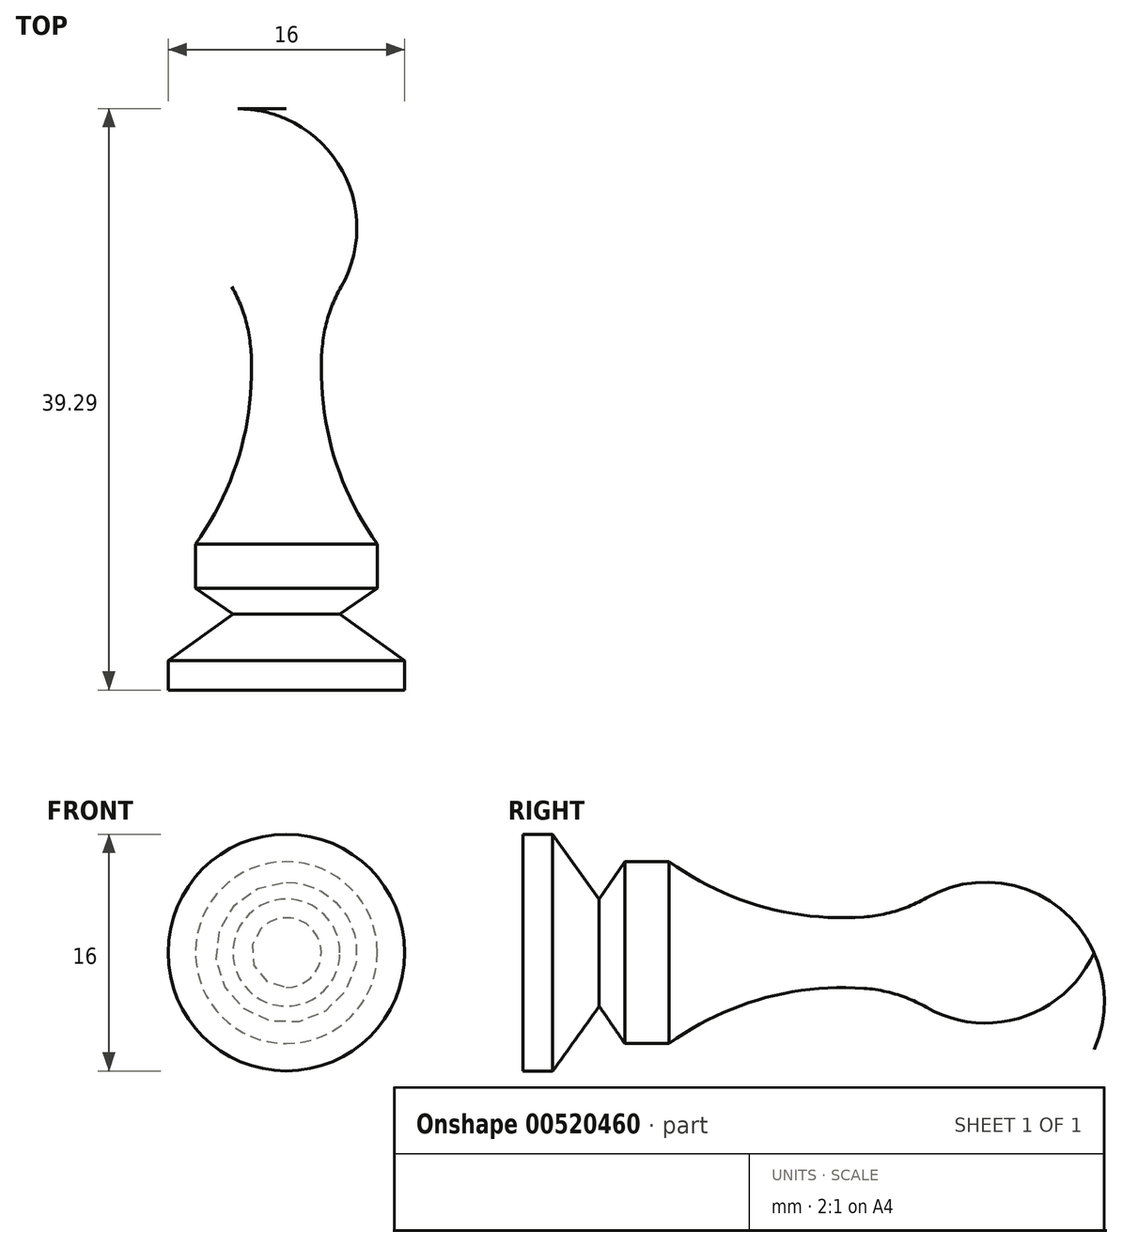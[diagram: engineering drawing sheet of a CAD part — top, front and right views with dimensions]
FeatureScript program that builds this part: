
annotation { "Feature Type Name" : "Feature", "Feature Type Description" : "" }
export const myFeature = defineFeature(function(context is Context, id is Id, definition is map)
    precondition{}
    {
        {
            var Q0;
            Q0=qCreatedBy(makeId("Top.planeOp"),FACE);
            var sketch = newSketch(context, id + "F0", { "sketchPlane" : qUnion([Q0])});
            skLineSegment(sketch, "E0", {"start": v(0, 0) * mm, "end": v(-8, 0) * mm});
            skLineSegment(sketch, "E1", {"start": v(-8, 0) * mm, "end": v(-8, 2) * mm});
            skLineSegment(sketch, "E2", {"start": v(-8, 2) * mm, "end": v(-3.62, 5.14) * mm});
            skLineSegment(sketch, "E3", {"start": v(-3.62, 5.14) * mm, "end": v(-6.15, 6.87) * mm});
            skLineSegment(sketch, "E4", {"start": v(-6.15, 6.87) * mm, "end": v(-6.15, 9.87) * mm});
            skLineSegment(sketch, "E5", {"start": v(0, 0) * mm, "end": v(0, 32) * mm});
            skLineSegment(sketch, "E6", {"start": v(0, 32) * mm, "end": v(0, 38.59) * mm});
            skArc(sketch, "E7", {"start": v(0, 38.59) * mm, "mid": v(-4.36, 33.75) * mm, "end": v(-3.7, 27.26) * mm});
            skArc(sketch, "E8", {"start": v(-6.15, 9.87) * mm, "mid": v(-3.12, 16.12) * mm, "end": v(-2.41, 23.02) * mm});
            skPoint(sketch, "E9.end.orphan", {"position": v(-3.62, 0) * mm});
            skPoint(sketch, "E10.end.orphan", {"position": v(-1.44, 0) * mm});
            skPoint(sketch, "E10.start.orphan", {"position": v(-1.44, 26.07) * mm});
            skPoint(sketch, "E11.end.orphan", {"position": v(0, 26.07) * mm});
            skPoint(sketch, "E12.visualSharp", {"position": v(-2.87, 26.07) * mm});
            skArc(sketch, "E12.filletArc", {"start": v(-2.41, 23.02) * mm, "mid": v(-2.82, 25.22) * mm, "end": v(-3.7, 27.26) * mm});
            skSolve(sketch);
        }
        {
            var Q0;
            Q0=makeQuery(id+"F0.imprint","IMPRINT",FACE,{"disambiguationData":[TD([[makeQuery(id+"F0.imprint","IMPRINT",EDGE,{"derivedFrom":sQuery(id+"F0.wireOp",EDGE,"E0")}),-1.0]])]});
            var Q1;
            Q1=sQuery(id+"F0.wireOp",EDGE,"E5");
            revolve(context, id + "F1", {"entities" : qUnion([Q0]), "axis" : qUnion([Q1]), "revolveType" : RevolveType.FULL});
        }
    });
